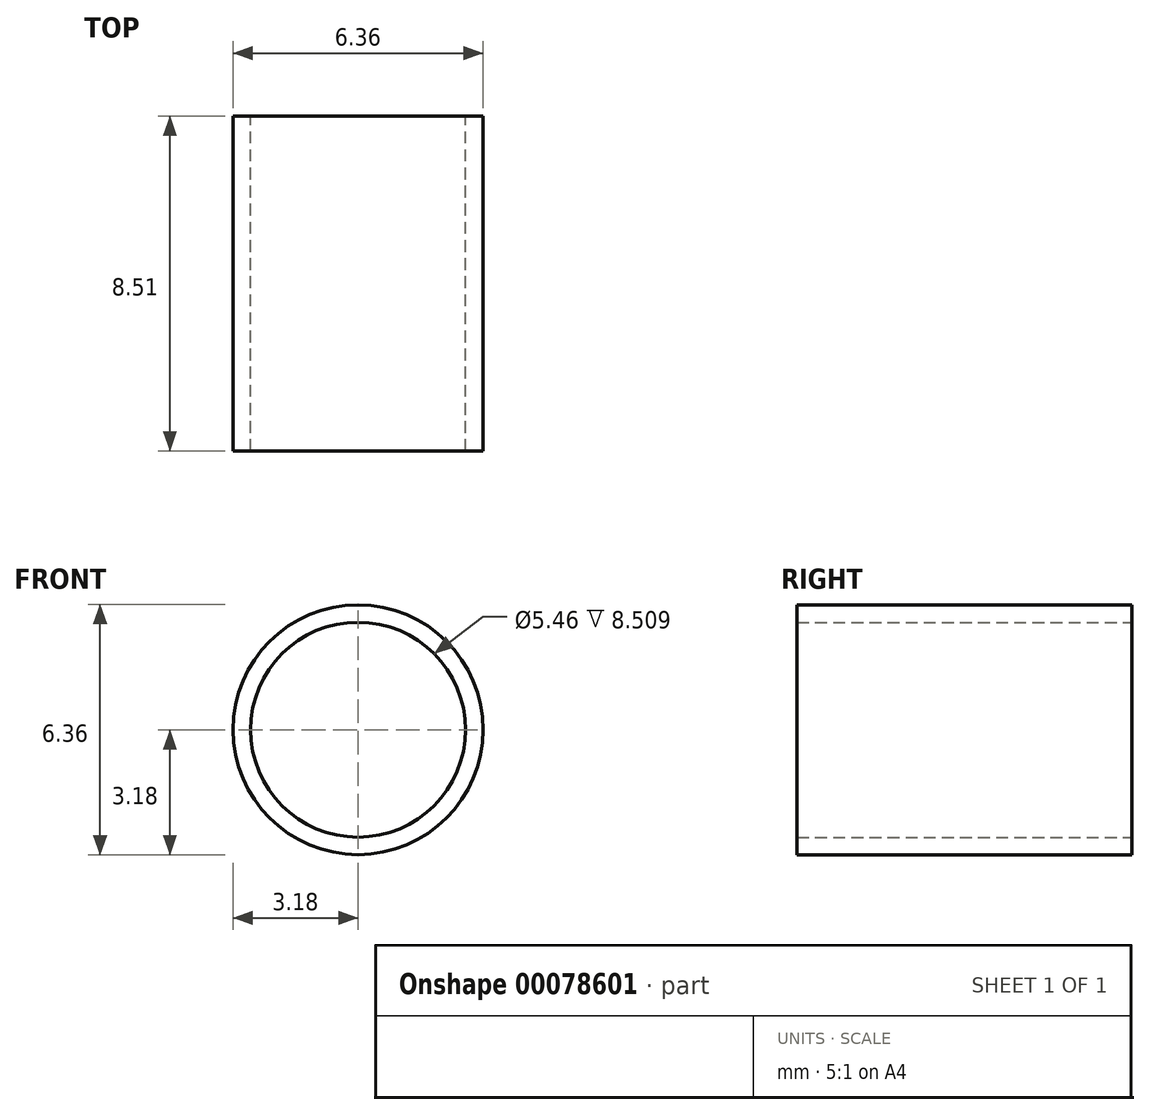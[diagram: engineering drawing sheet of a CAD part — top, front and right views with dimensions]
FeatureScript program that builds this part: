
annotation { "Feature Type Name" : "Feature", "Feature Type Description" : "" }
export const myFeature = defineFeature(function(context is Context, id is Id, definition is map)
    precondition{}
    {
        {
            var Q0;
            Q0=qCreatedBy(makeId("Front.planeOp"),FACE);
            var sketch = newSketch(context, id + "F0", { "sketchPlane" : qUnion([Q0])});
            skCircle(sketch, "E0", {"center": v(0, 0) * mm, "radius": 3.18 * mm});
            skCircle(sketch, "E1", {"center": v(0, 0) * mm, "radius": 2.73 * mm});
            skSolve(sketch);
        }
        {
            var Q0;
            Q0=makeQuery(id+"F0.imprint","IMPRINT",FACE,{"disambiguationData":[TD([[makeQuery(id+"F0.imprint","IMPRINT",EDGE,{"derivedFrom":sQuery(id+"F0.wireOp",EDGE,"E0")}),1.0]])]});
            extrude(context, id + "F1", {"entities" : qUnion([Q0]), "depth" : 8.5 * mm});
        }
    });
